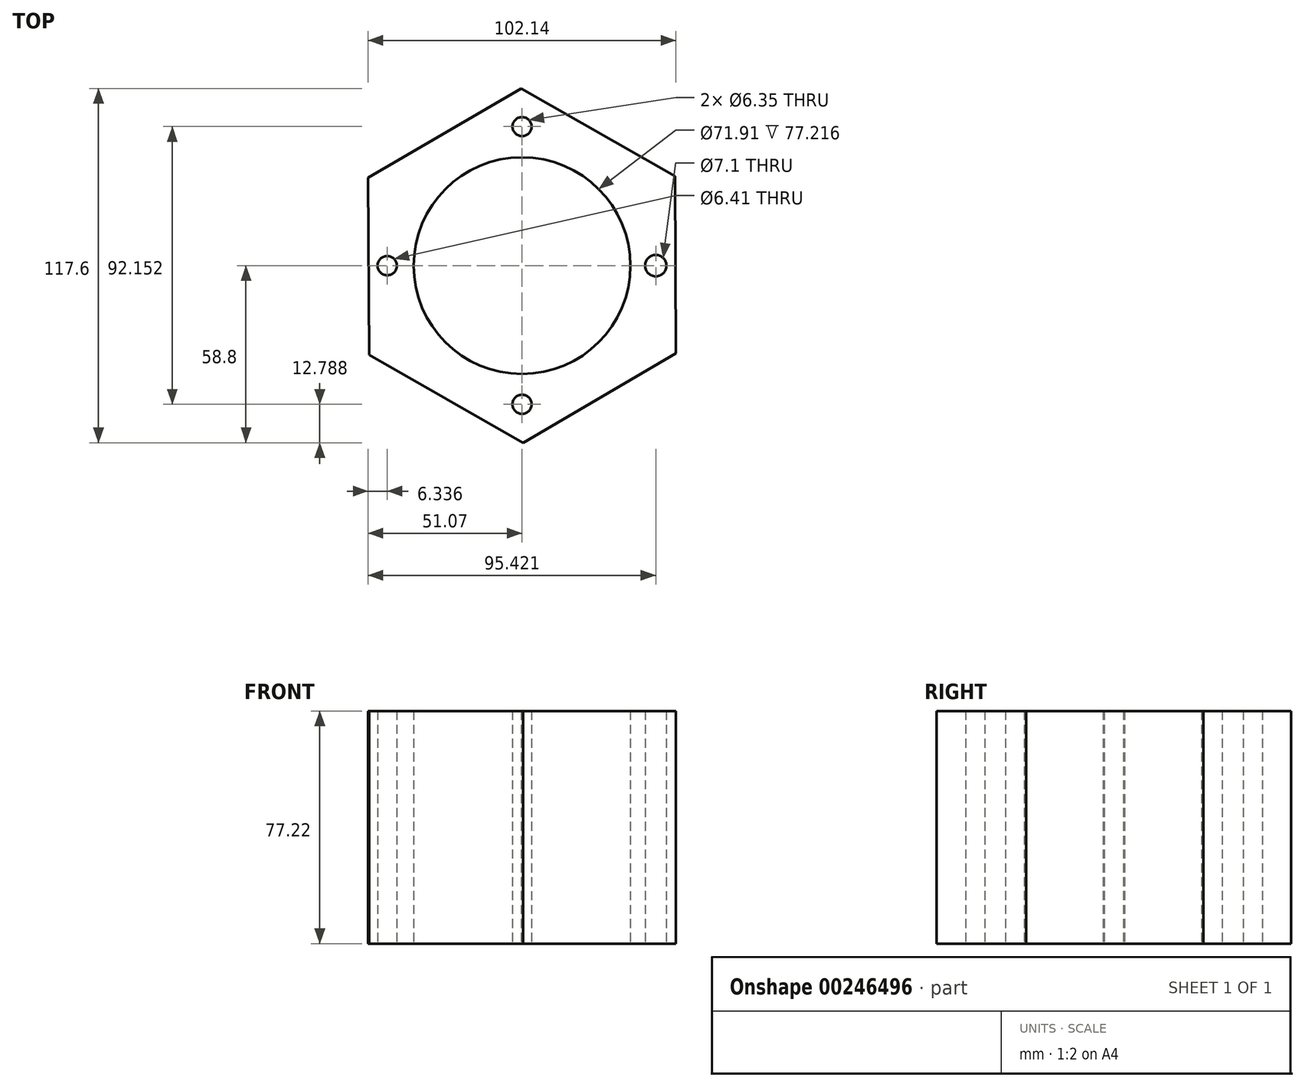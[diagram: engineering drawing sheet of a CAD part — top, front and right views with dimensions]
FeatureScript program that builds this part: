
annotation { "Feature Type Name" : "Feature", "Feature Type Description" : "" }
export const myFeature = defineFeature(function(context is Context, id is Id, definition is map)
    precondition{}
    {
        {
            var Q0;
            Q0=qCreatedBy(makeId("Top.planeOp"),FACE);
            var sketch = newSketch(context, id + "F0", { "sketchPlane" : qUnion([Q0])});
            skCircle(sketch, "E0.cCircle", {"center": v(0, 0) * mm, "radius": 50.92 * mm, "construction": true});
            skLineSegment(sketch, "E0.0", {"start": v(51.07, -29.13) * mm, "end": v(0.3, -58.8) * mm});
            skLineSegment(sketch, "E0.1", {"start": v(0.3, -58.8) * mm, "end": v(-50.77, -29.66) * mm});
            skLineSegment(sketch, "E0.2", {"start": v(-50.77, -29.66) * mm, "end": v(-51.07, 29.13) * mm});
            skLineSegment(sketch, "E0.3", {"start": v(-51.07, 29.13) * mm, "end": v(-0.3, 58.8) * mm});
            skLineSegment(sketch, "E0.4", {"start": v(-0.3, 58.8) * mm, "end": v(50.77, 29.66) * mm});
            skLineSegment(sketch, "E0.5", {"start": v(50.77, 29.66) * mm, "end": v(51.07, -29.13) * mm});
            skPoint(sketch, "E0.0.midPoint", {"position": v(25.7, -43.97) * mm});
            skSolve(sketch);
        }
        {
            var Q0;
            Q0=makeQuery(id+"F0.imprint","IMPRINT",FACE,{"disambiguationData":[TD([[makeQuery(id+"F0.imprint","IMPRINT",EDGE,{"derivedFrom":sQuery(id+"F0.wireOp",EDGE,"E0.0")}),-1.0]])]});
            extrude(context, id + "F1", {"entities" : qUnion([Q0]), "depth" : 77.22 * mm});
        }
        {
            var Q0;
            Q0=qCreatedBy(makeId("Top.planeOp"),FACE);
            var sketch = newSketch(context, id + "F2", { "sketchPlane" : qUnion([Q0])});
            skCircle(sketch, "E1", {"center": v(0, 0) * mm, "radius": 35.96 * mm});
            skLineSegment(sketch, "E2", {"start": v(0, -51.9) * mm, "end": v(45.12, -25.82) * mm});
            skLineSegment(sketch, "E3", {"start": v(45.12, -25.82) * mm, "end": v(38.35, -14.12) * mm});
            skLineSegment(sketch, "E4", {"start": v(38.35, -14.12) * mm, "end": v(20.32, -34.5) * mm});
            skLineSegment(sketch, "E5", {"start": v(20.32, -34.5) * mm, "end": v(0, -40.13) * mm});
            skLineSegment(sketch, "E6", {"start": v(0, -40.13) * mm, "end": v(0, -51.9) * mm});
            skLineSegment(sketch, "E7", {"start": v(-41.28, 0) * mm, "end": v(-29.01, 28.63) * mm});
            skLineSegment(sketch, "E8", {"start": v(-29.01, 28.63) * mm, "end": v(0, 41.92) * mm});
            skLineSegment(sketch, "E9", {"start": v(0, 41.92) * mm, "end": v(0, 53.94) * mm});
            skLineSegment(sketch, "E10", {"start": v(0, 53.94) * mm, "end": v(-45.5, 27.64) * mm});
            skLineSegment(sketch, "E11", {"start": v(-45.5, 27.64) * mm, "end": v(-48.95, 0) * mm});
            skLineSegment(sketch, "E12", {"start": v(-48.95, 0) * mm, "end": v(-41.28, 0) * mm});
            skLineSegment(sketch, "E13", {"start": v(7.54, 40.13) * mm, "end": v(37.96, 21.73) * mm});
            skLineSegment(sketch, "E14", {"start": v(37.96, 21.73) * mm, "end": v(40, -7.67) * mm});
            skLineSegment(sketch, "E15", {"start": v(40, -7.67) * mm, "end": v(48.28, -8.7) * mm});
            skLineSegment(sketch, "E16", {"start": v(48.28, -8.7) * mm, "end": v(48.28, 25.05) * mm});
            skLineSegment(sketch, "E17", {"start": v(48.28, 25.05) * mm, "end": v(9.33, 48.82) * mm});
            skLineSegment(sketch, "E18", {"start": v(9.33, 48.82) * mm, "end": v(7.54, 40.13) * mm});
            skLineSegment(sketch, "E19", {"start": v(-41.03, -4.86) * mm, "end": v(-47.93, -4.86) * mm});
            skLineSegment(sketch, "E20", {"start": v(-47.93, -4.86) * mm, "end": v(-47.93, -25.82) * mm});
            skLineSegment(sketch, "E21", {"start": v(-47.93, -25.82) * mm, "end": v(-4.98, -50.36) * mm});
            skLineSegment(sketch, "E22", {"start": v(-4.98, -50.36) * mm, "end": v(-4.98, -39.88) * mm});
            skLineSegment(sketch, "E23", {"start": v(-4.98, -39.88) * mm, "end": v(-32.08, -24.8) * mm});
            skLineSegment(sketch, "E24", {"start": v(-32.08, -24.8) * mm, "end": v(-41.03, -4.86) * mm});
            skSolve(sketch);
        }
        {
            var Q0;
            Q0=makeQuery(id+"F2.imprint","IMPRINT",FACE,{"disambiguationData":[TD([[makeQuery(id+"F2.imprint","IMPRINT",EDGE,{"derivedFrom":sQuery(id+"F2.wireOp",EDGE,"E1")}),1.0]])]});
            var Q1;
            Q1=sQuery(id+"F2.wireOp",EDGE,"E1");
            extrude(context, id + "F3", {"entities" : qUnion([Q0]), "operationType" : NewBodyOperationType.REMOVE, "surfaceEntities" : qUnion([Q1]), "depth" : 87.88 * mm});
        }
        {
            var Q0;
            Q0=qCreatedBy(makeId("Top.planeOp"),FACE);
            var sketch = newSketch(context, id + "F4", { "sketchPlane" : qUnion([Q0])});
            skCircle(sketch, "E25", {"center": v(0, -46.01) * mm, "radius": 3.17 * mm});
            skCircle(sketch, "E26", {"center": v(-44.73, 0) * mm, "radius": 3.2 * mm});
            skCircle(sketch, "E27", {"center": v(44.35, 0) * mm, "radius": 3.55 * mm});
            skCircle(sketch, "E28", {"center": v(0, 46.14) * mm, "radius": 3.17 * mm});
            skSolve(sketch);
        }
        {
            var Q0;
            Q0=makeQuery(id+"F4.imprint","IMPRINT",FACE,{"disambiguationData":[TD([[makeQuery(id+"F4.imprint","IMPRINT",EDGE,{"derivedFrom":sQuery(id+"F4.wireOp",EDGE,"E26")}),1.0]])]});
            var Q1;
            Q1=makeQuery(id+"F4.imprint","IMPRINT",FACE,{"disambiguationData":[TD([[makeQuery(id+"F4.imprint","IMPRINT",EDGE,{"derivedFrom":sQuery(id+"F4.wireOp",EDGE,"E27")}),1.0]])]});
            var Q2;
            Q2=makeQuery(id+"F4.imprint","IMPRINT",FACE,{"disambiguationData":[TD([[makeQuery(id+"F4.imprint","IMPRINT",EDGE,{"derivedFrom":sQuery(id+"F4.wireOp",EDGE,"E28")}),1.0]])]});
            var Q3;
            Q3=makeQuery(id+"F4.imprint","IMPRINT",FACE,{"disambiguationData":[TD([[makeQuery(id+"F4.imprint","IMPRINT",EDGE,{"derivedFrom":sQuery(id+"F4.wireOp",EDGE,"E25")}),1.0]])]});
            extrude(context, id + "F5", {"entities" : qUnion([Q0, Q1, Q2, Q3]), "operationType" : NewBodyOperationType.REMOVE, "depth" : 95.5 * mm});
        }
    });
